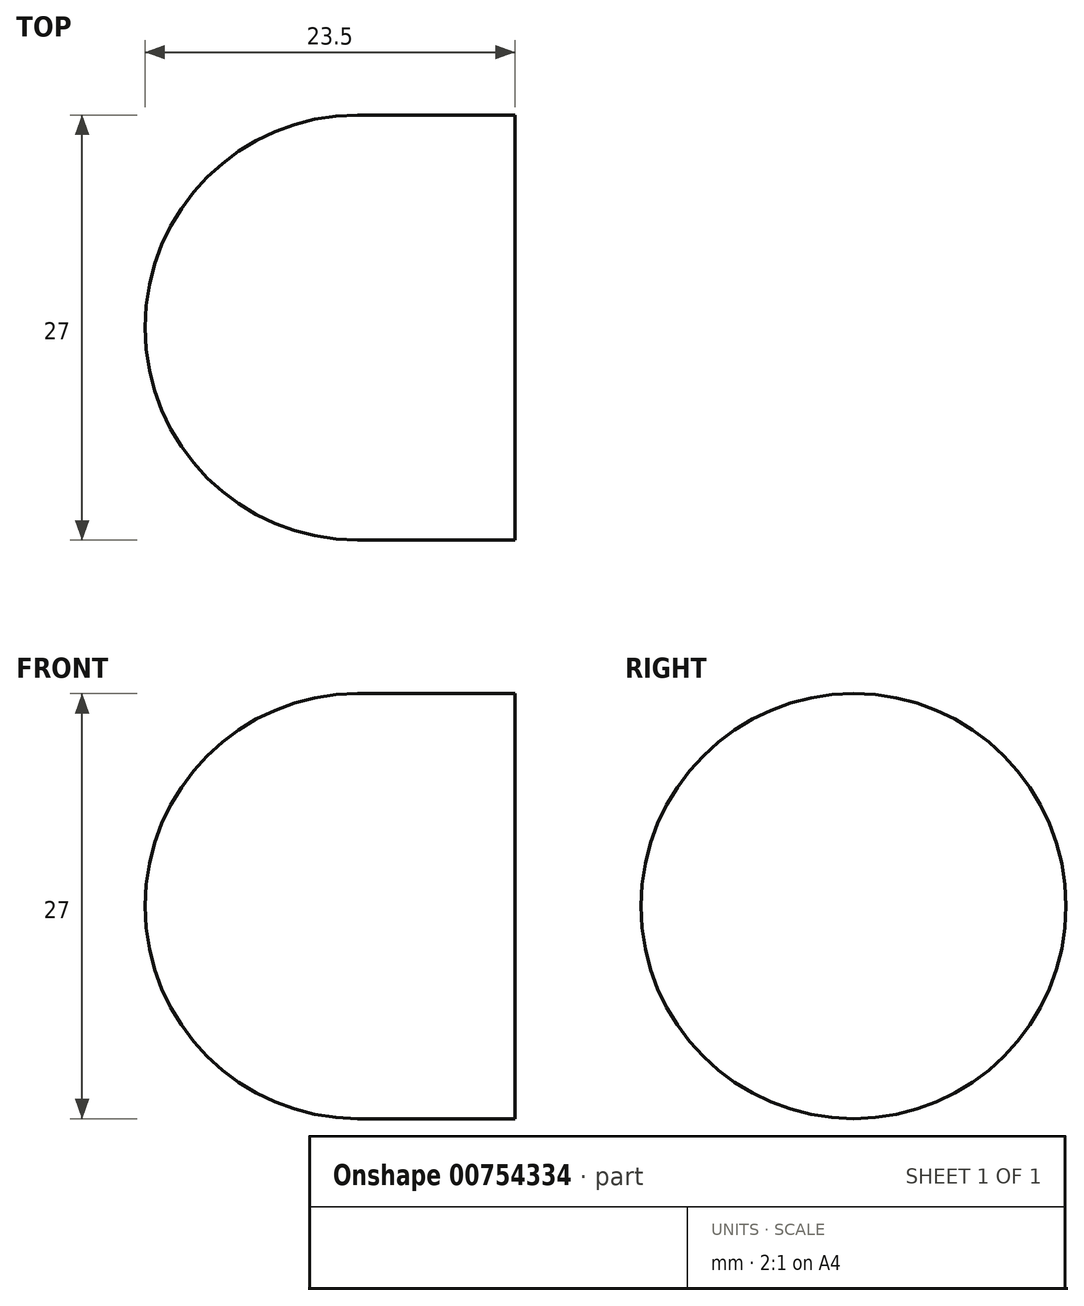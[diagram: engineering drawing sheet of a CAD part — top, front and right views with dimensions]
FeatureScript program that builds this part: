
annotation { "Feature Type Name" : "Feature", "Feature Type Description" : "" }
export const myFeature = defineFeature(function(context is Context, id is Id, definition is map)
    precondition{}
    {
        {
            var Q0;
            Q0=qCreatedBy(makeId("Right.planeOp"),FACE);
            var sketch = newSketch(context, id + "F0", { "sketchPlane" : qUnion([Q0])});
            skCircle(sketch, "E0", {"center": v(0, 0) * mm, "radius": 13.5 * mm});
            skSolve(sketch);
        }
        {
            var Q0;
            Q0 = qSketchRegion(id + "F0", true);
            extrude(context, id + "F1", {"entities" : qUnion([Q0]), "depth" : 10 * mm, "offsetDistance" : 25 * mm});
        }
        {
            var Q0;
            Q0=makeQuery(id+"F1.opExtrude","CAP_FACE",FACE,{"disambiguationData":[OSD([sQuery(id+"F0.wireOp",EDGE,"E0")])],"isStart":true});
            var sketch = newSketch(context, id + "F2", { "sketchPlane" : qUnion([Q0])});
            skArc(sketch, "E1", {"start": v(0, 13.5) * mm, "mid": v(13.5, 0) * mm, "end": v(0, -13.5) * mm});
            skLineSegment(sketch, "E2", {"start": v(0, 13.5) * mm, "end": v(0, -13.5) * mm});
            skSolve(sketch);
        }
        {
            var Q0;
            Q0 = qSketchRegion(id + "F2", true);
            var Q1;
            Q1=sQuery(id+"F2.wireOp",EDGE,"E2");
            revolve(context, id + "F3", {"operationType" : NewBodyOperationType.ADD, "surfaceOperationType" : NewSurfaceOperationType.NEW, "entities" : qUnion([Q0]), "axis" : qUnion([Q1]), "revolveType" : RevolveType.ONE_DIRECTION, "angle" : 180 * degree});
        }
    });
